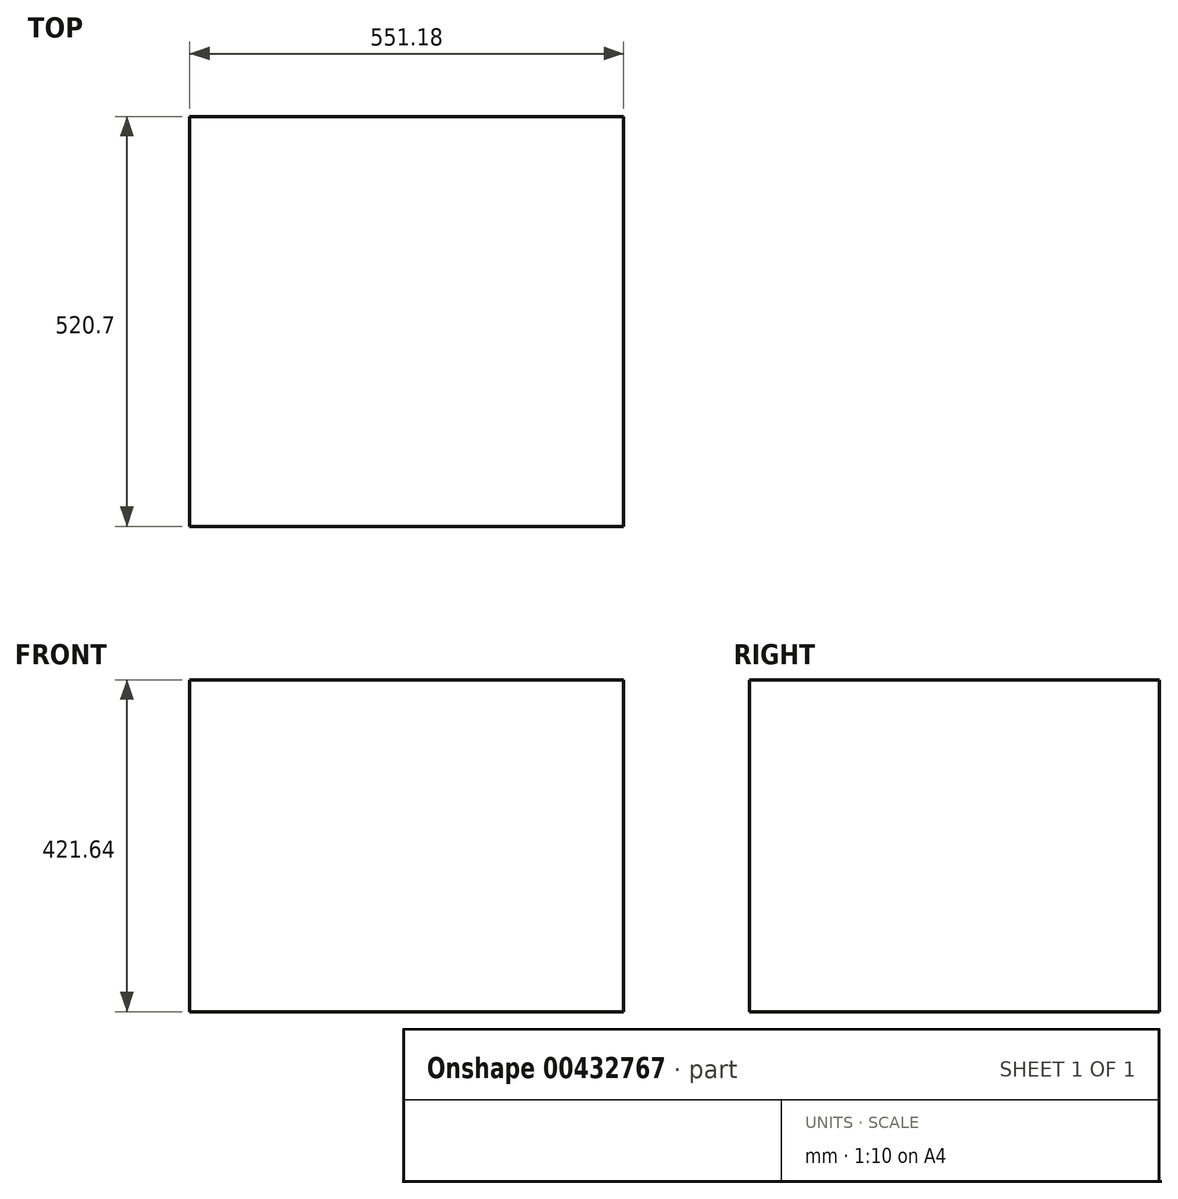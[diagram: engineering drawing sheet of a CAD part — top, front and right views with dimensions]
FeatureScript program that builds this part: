
annotation { "Feature Type Name" : "Feature", "Feature Type Description" : "" }
export const myFeature = defineFeature(function(context is Context, id is Id, definition is map)
    precondition{}
    {
        {
            var Q0;
            Q0=qCreatedBy(makeId("Front.planeOp"),FACE);
            var sketch = newSketch(context, id + "F0", { "sketchPlane" : qUnion([Q0])});
            skLineSegment(sketch, "E0.bottom", {"start": v(0, 0) * mm, "end": v(551.18, 0) * mm});
            skLineSegment(sketch, "E0.top", {"start": v(0, 421.64) * mm, "end": v(551.18, 421.64) * mm});
            skLineSegment(sketch, "E0.left", {"start": v(0, 0) * mm, "end": v(0, 421.64) * mm});
            skLineSegment(sketch, "E0.right", {"start": v(551.18, 0) * mm, "end": v(551.18, 421.64) * mm});
            skLineSegment(sketch, "E1.bottom", {"start": v(551.18, 421.64) * mm, "end": v(551.18, 421.64) * mm});
            skLineSegment(sketch, "E1.left", {"start": v(551.18, 421.64) * mm, "end": v(551.18, 399.42) * mm});
            skLineSegment(sketch, "E1.right", {"start": v(551.18, 421.64) * mm, "end": v(551.18, 399.42) * mm});
            skSolve(sketch);
        }
        {
            var Q0;
            Q0=makeQuery(id+"F0.imprint","IMPRINT",FACE,{"disambiguationData":[TD([[makeQuery(id+"F0.imprint","IMPRINT",EDGE,{"derivedFrom":sQuery(id+"F0.wireOp",EDGE,"E0.bottom")}),1.0]])]});
            extrude(context, id + "F1", {"entities" : qUnion([Q0]), "depth" : 520.7 * mm});
        }
    });
